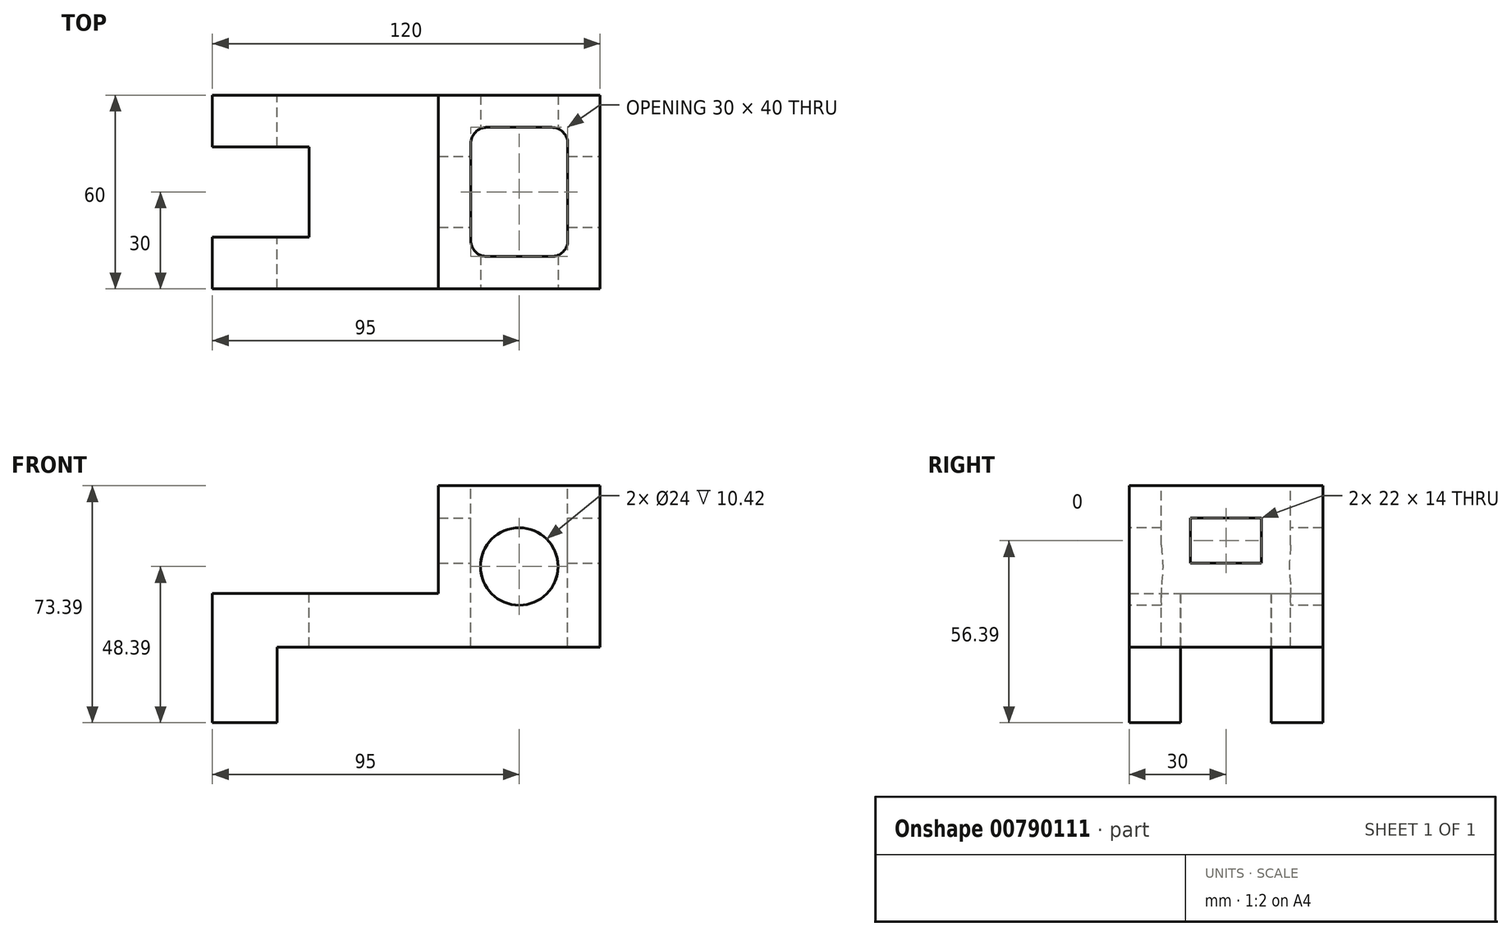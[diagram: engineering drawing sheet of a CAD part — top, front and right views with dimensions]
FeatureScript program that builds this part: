
annotation { "Feature Type Name" : "Feature", "Feature Type Description" : "" }
export const myFeature = defineFeature(function(context is Context, id is Id, definition is map)
    precondition{}
    {
        {
            var Q0;
            Q0=qCreatedBy(makeId("Front.planeOp"),FACE);
            var sketch = newSketch(context, id + "F0", { "sketchPlane" : qUnion([Q0])});
            skLineSegment(sketch, "E0.bottom", {"start": v(-25, -25) * mm, "end": v(25, -25) * mm});
            skLineSegment(sketch, "E0.top", {"start": v(-25, 25) * mm, "end": v(25, 25) * mm});
            skLineSegment(sketch, "E0.left", {"start": v(-25, -25) * mm, "end": v(-25, 25) * mm});
            skLineSegment(sketch, "E0.right", {"start": v(25, -25) * mm, "end": v(25, 25) * mm});
            skPoint(sketch, "E0.middle", {"position": v(0, 0) * mm});
            skLineSegment(sketch, "E1", {"start": v(-25, -25) * mm, "end": v(-75, -25) * mm});
            skLineSegment(sketch, "E2", {"start": v(-75, -25) * mm, "end": v(-75, -48.39) * mm});
            skLineSegment(sketch, "E3", {"start": v(-75, -48.39) * mm, "end": v(-95, -48.39) * mm});
            skLineSegment(sketch, "E4", {"start": v(-95, -48.39) * mm, "end": v(-95, -8.39) * mm});
            skLineSegment(sketch, "E5", {"start": v(-95, -8.39) * mm, "end": v(-25, -8.39) * mm});
            skSolve(sketch);
        }
        {
            var Q0;
            Q0 = qSketchRegion(id + "F0", true);
            extrude(context, id + "F1", {"entities" : qUnion([Q0]), "depth" : 60 * mm, "offsetDistance" : 25.4 * mm});
        }
        {
            var Q0;
            Q0=makeQuery(id+"F1.opExtrude","CAP_FACE",FACE,{"disambiguationData":[OSD([sQuery(id+"F0.wireOp",EDGE,"E0.bottom"),sQuery(id+"F0.wireOp",EDGE,"E0.top"),sQuery(id+"F0.wireOp",EDGE,"E0.left"),sQuery(id+"F0.wireOp",EDGE,"E0.right"),sQuery(id+"F0.wireOp",EDGE,"E1"),sQuery(id+"F0.wireOp",EDGE,"E2"),sQuery(id+"F0.wireOp",EDGE,"E3"),sQuery(id+"F0.wireOp",EDGE,"E4"),sQuery(id+"F0.wireOp",EDGE,"E5")])],"isStart":false});
            var sketch = newSketch(context, id + "F2", { "sketchPlane" : qUnion([Q0])});
            skCircle(sketch, "E6", {"center": v(0, 0) * mm, "radius": 12 * mm});
            skSolve(sketch);
        }
        {
            var Q0;
            Q0 = qSketchRegion(id + "F2", true);
            extrude(context, id + "F3", {"entities" : qUnion([Q0]), "operationType" : NewBodyOperationType.REMOVE, "endBound" : BoundingType.THROUGH_ALL, "oppositeDirection" : true, "depth" : 25.4 * mm, "offsetDistance" : 25.4 * mm});
        }
        {
            var Q0;
            Q0=makeQuery(id+"F1.opExtrude","SWEPT_FACE",FACE,{"disambiguationData":[OSD([sQuery(id+"F0.wireOp",EDGE,"E5")])]});
            var sketch = newSketch(context, id + "F4", { "sketchPlane" : qUnion([Q0])});
            skPoint(sketch, "E7.end.orphan", {"position": v(-95, -18.56) * mm});
            skLineSegment(sketch, "E8.bottom", {"start": v(-65, -44) * mm, "end": v(-125, -44) * mm});
            skLineSegment(sketch, "E8.top", {"start": v(-65, -16) * mm, "end": v(-125, -16) * mm});
            skLineSegment(sketch, "E8.left", {"start": v(-65, -44) * mm, "end": v(-65, -16) * mm});
            skLineSegment(sketch, "E8.right", {"start": v(-125, -44) * mm, "end": v(-125, -16) * mm});
            skPoint(sketch, "E8.middle", {"position": v(-95, -30) * mm});
            skLineSegment(sketch, "E9", {"start": v(-95, -44) * mm, "end": v(-65, -44) * mm});
            skLineSegment(sketch, "E10.bottom", {"start": v(-10, -50) * mm, "end": v(10, -50) * mm});
            skLineSegment(sketch, "E10.top", {"start": v(-10, -10) * mm, "end": v(10, -10) * mm});
            skLineSegment(sketch, "E10.left", {"start": v(-15, -45) * mm, "end": v(-15, -15) * mm});
            skLineSegment(sketch, "E10.right", {"start": v(15, -45) * mm, "end": v(15, -15) * mm});
            skPoint(sketch, "E10.middle", {"position": v(0, -30) * mm});
            skPoint(sketch, "E10.middle.positionSnap0", {"position": v(-25, -30) * mm});
            skPoint(sketch, "E10.centerSnap0", {"position": v(-25, -30) * mm});
            skPoint(sketch, "E11.visualSharp", {"position": v(-15, -10) * mm});
            skArc(sketch, "E11.filletArc", {"start": v(-10, -10) * mm, "mid": v(-13.54, -11.46) * mm, "end": v(-15, -15) * mm});
            skPoint(sketch, "E12.visualSharp", {"position": v(15, -10) * mm});
            skArc(sketch, "E12.filletArc", {"start": v(15, -15) * mm, "mid": v(13.54, -11.46) * mm, "end": v(10, -10) * mm});
            skPoint(sketch, "E13.visualSharp", {"position": v(15, -50) * mm});
            skArc(sketch, "E13.filletArc", {"start": v(10, -50) * mm, "mid": v(13.54, -48.54) * mm, "end": v(15, -45) * mm});
            skPoint(sketch, "E14.visualSharp", {"position": v(-15, -50) * mm});
            skArc(sketch, "E14.filletArc", {"start": v(-15, -45) * mm, "mid": v(-13.54, -48.54) * mm, "end": v(-10, -50) * mm});
            skSolve(sketch);
        }
        {
            var Q0;
            Q0 = qSketchRegion(id + "F4", true);
            extrude(context, id + "F5", {"entities" : qUnion([Q0]), "operationType" : NewBodyOperationType.REMOVE, "endBound" : BoundingType.THROUGH_ALL, "oppositeDirection" : true, "depth" : 25.4 * mm, "offsetDistance" : 25.4 * mm});
        }
        {
            var Q0;
            Q0=makeQuery(id+"F1.opExtrude","SWEPT_FACE",FACE,{"disambiguationData":[OSD([sQuery(id+"F0.wireOp",EDGE,"E0.top")])]});
            var sketch = newSketch(context, id + "F6", { "sketchPlane" : qUnion([Q0])});
            skLineSegment(sketch, "E15.bottom", {"start": v(-10, -50) * mm, "end": v(10, -50) * mm});
            skLineSegment(sketch, "E15.top", {"start": v(-10, -10) * mm, "end": v(10, -10) * mm});
            skLineSegment(sketch, "E15.left", {"start": v(-15, -45) * mm, "end": v(-15, -15) * mm});
            skLineSegment(sketch, "E15.right", {"start": v(15, -45) * mm, "end": v(15, -15) * mm});
            skPoint(sketch, "E15.middle", {"position": v(0, -30) * mm});
            skPoint(sketch, "E15.middle.positionSnap0", {"position": v(-25, -30) * mm});
            skPoint(sketch, "E15.centerSnap0", {"position": v(-25, -30) * mm});
            skPoint(sketch, "E16.visualSharp", {"position": v(-15, -10) * mm});
            skArc(sketch, "E16.filletArc", {"start": v(-10, -10) * mm, "mid": v(-13.54, -11.46) * mm, "end": v(-15, -15) * mm});
            skPoint(sketch, "E17.visualSharp", {"position": v(15, -10) * mm});
            skArc(sketch, "E17.filletArc", {"start": v(15, -15) * mm, "mid": v(13.54, -11.46) * mm, "end": v(10, -10) * mm});
            skPoint(sketch, "E18.visualSharp", {"position": v(15, -50) * mm});
            skArc(sketch, "E18.filletArc", {"start": v(10, -50) * mm, "mid": v(13.54, -48.54) * mm, "end": v(15, -45) * mm});
            skPoint(sketch, "E19.visualSharp", {"position": v(-15, -50) * mm});
            skArc(sketch, "E19.filletArc", {"start": v(-15, -45) * mm, "mid": v(-13.54, -48.54) * mm, "end": v(-10, -50) * mm});
            skSolve(sketch);
        }
        {
            var Q0;
            Q0 = qSketchRegion(id + "F6", true);
            extrude(context, id + "F7", {"entities" : qUnion([Q0]), "operationType" : NewBodyOperationType.REMOVE, "endBound" : BoundingType.THROUGH_ALL, "oppositeDirection" : true, "depth" : 25.4 * mm, "offsetDistance" : 25.4 * mm});
        }
        {
            var Q0;
            Q0=makeQuery(id+"F1.opExtrude","SWEPT_FACE",FACE,{"disambiguationData":[OSD([sQuery(id+"F0.wireOp",EDGE,"E0.right")])]});
            var sketch = newSketch(context, id + "F8", { "sketchPlane" : qUnion([Q0])});
            skLineSegment(sketch, "E20", {"start": v(-60, -25) * mm, "end": v(-41, -25) * mm});
            skLineSegment(sketch, "E21", {"start": v(-41, -25) * mm, "end": v(-19, -25) * mm});
            skLineSegment(sketch, "E22", {"start": v(-19, -25) * mm, "end": v(0, -25) * mm});
            skLineSegment(sketch, "E23", {"start": v(-41, -25) * mm, "end": v(-41, 1) * mm});
            skLineSegment(sketch, "E24.bottom", {"start": v(-41, 1) * mm, "end": v(-19, 1) * mm});
            skLineSegment(sketch, "E24.top", {"start": v(-41, 15) * mm, "end": v(-19, 15) * mm});
            skLineSegment(sketch, "E24.left", {"start": v(-41, 1) * mm, "end": v(-41, 15) * mm});
            skLineSegment(sketch, "E24.right", {"start": v(-19, 1) * mm, "end": v(-19, 15) * mm});
            skSolve(sketch);
        }
        {
            var Q0;
            Q0 = qSketchRegion(id + "F8", true);
            extrude(context, id + "F9", {"entities" : qUnion([Q0]), "operationType" : NewBodyOperationType.REMOVE, "endBound" : BoundingType.THROUGH_ALL, "oppositeDirection" : true, "depth" : 25.4 * mm, "offsetDistance" : 25.4 * mm});
        }
    });
